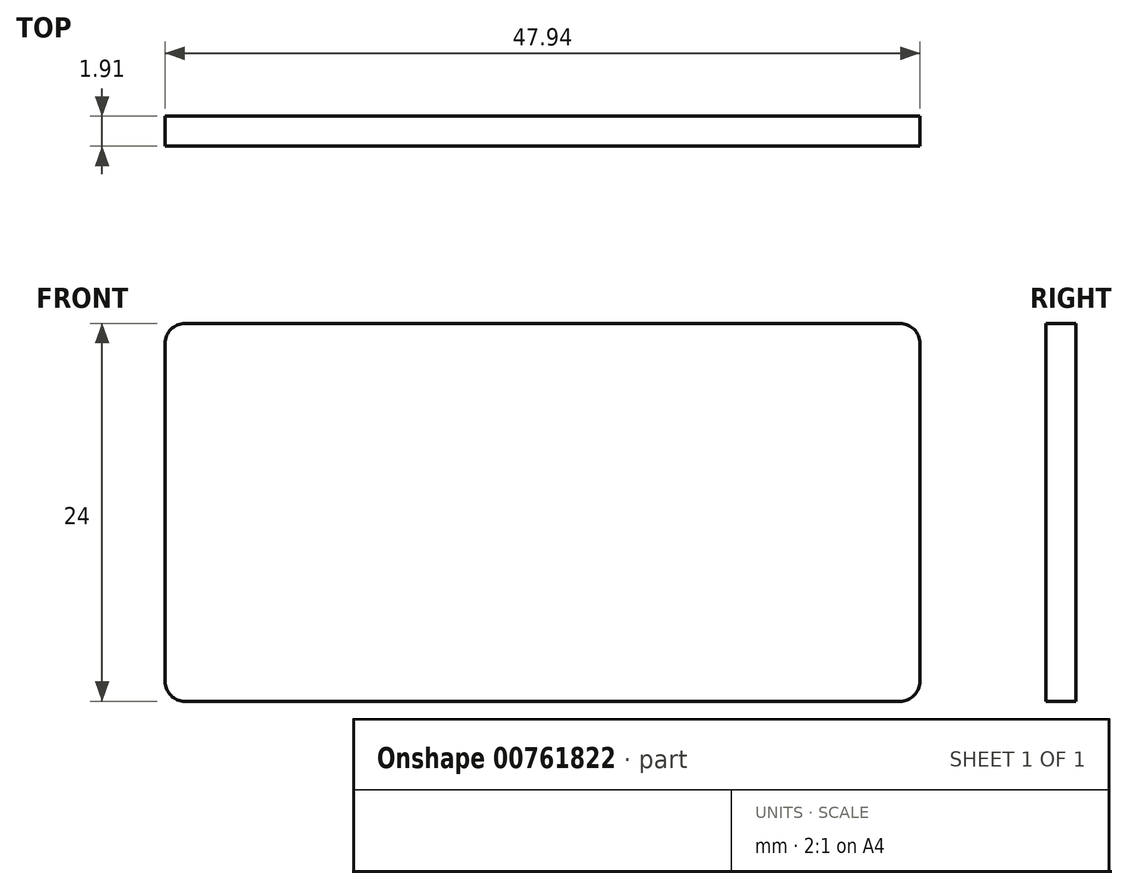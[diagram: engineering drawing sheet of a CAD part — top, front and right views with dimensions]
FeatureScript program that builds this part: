
annotation { "Feature Type Name" : "Feature", "Feature Type Description" : "" }
export const myFeature = defineFeature(function(context is Context, id is Id, definition is map)
    precondition{}
    {
        {
            var Q0;
            Q0=qCreatedBy(makeId("Front.planeOp"),FACE);
            var sketch = newSketch(context, id + "F0", { "sketchPlane" : qUnion([Q0])});
            skLineSegment(sketch, "E0.bottom", {"start": v(-23.97, 12) * mm, "end": v(23.97, 12) * mm});
            skLineSegment(sketch, "E0.top", {"start": v(-23.97, -12) * mm, "end": v(23.97, -12) * mm});
            skLineSegment(sketch, "E0.left", {"start": v(-23.97, 12) * mm, "end": v(-23.97, -12) * mm});
            skLineSegment(sketch, "E0.right", {"start": v(23.97, 12) * mm, "end": v(23.97, -12) * mm});
            skPoint(sketch, "E0.middle", {"position": v(0, 0) * mm});
            skSolve(sketch);
        }
        {
            var Q0;
            Q0 = qSketchRegion(id + "F0", true);
            extrude(context, id + "F1", {"entities" : qUnion([Q0]), "depth" : 1.9 * mm, "offsetDistance" : 25.4 * mm});
        }
        {
            var Q0;
            Q0=makeQuery(id+"F1.opExtrude","SWEPT_EDGE",EDGE,{"disambiguationData":[OSD([sQuery(id+"F0.wireOp",EDGE,"E0.bottom"),sQuery(id+"F0.wireOp",EDGE,"E0.left")])]});
            fillet(context, id + "F2", {"entities" : qUnion([Q0]), "radius" : 1.27 * mm, "tangentPropagation" : true, "allowEdgeOverflow" : false});
        }
        {
            var Q0;
            Q0=makeQuery(id+"F1.opExtrude","SWEPT_EDGE",EDGE,{"disambiguationData":[OSD([sQuery(id+"F0.wireOp",EDGE,"E0.bottom"),sQuery(id+"F0.wireOp",EDGE,"E0.right")])]});
            fillet(context, id + "F3", {"entities" : qUnion([Q0]), "radius" : 1.27 * mm, "tangentPropagation" : true, "allowEdgeOverflow" : false});
        }
        {
            var Q0;
            Q0=makeQuery(id+"F1.opExtrude","SWEPT_EDGE",EDGE,{"disambiguationData":[OSD([sQuery(id+"F0.wireOp",EDGE,"E0.top"),sQuery(id+"F0.wireOp",EDGE,"E0.right")])]});
            fillet(context, id + "F4", {"entities" : qUnion([Q0]), "radius" : 1.27 * mm, "tangentPropagation" : true, "allowEdgeOverflow" : false});
        }
        {
            var Q0;
            Q0=makeQuery(id+"F1.opExtrude","SWEPT_EDGE",EDGE,{"disambiguationData":[OSD([sQuery(id+"F0.wireOp",EDGE,"E0.top"),sQuery(id+"F0.wireOp",EDGE,"E0.left")])]});
            fillet(context, id + "F5", {"entities" : qUnion([Q0]), "radius" : 1.27 * mm, "tangentPropagation" : true, "allowEdgeOverflow" : false});
        }
    });
